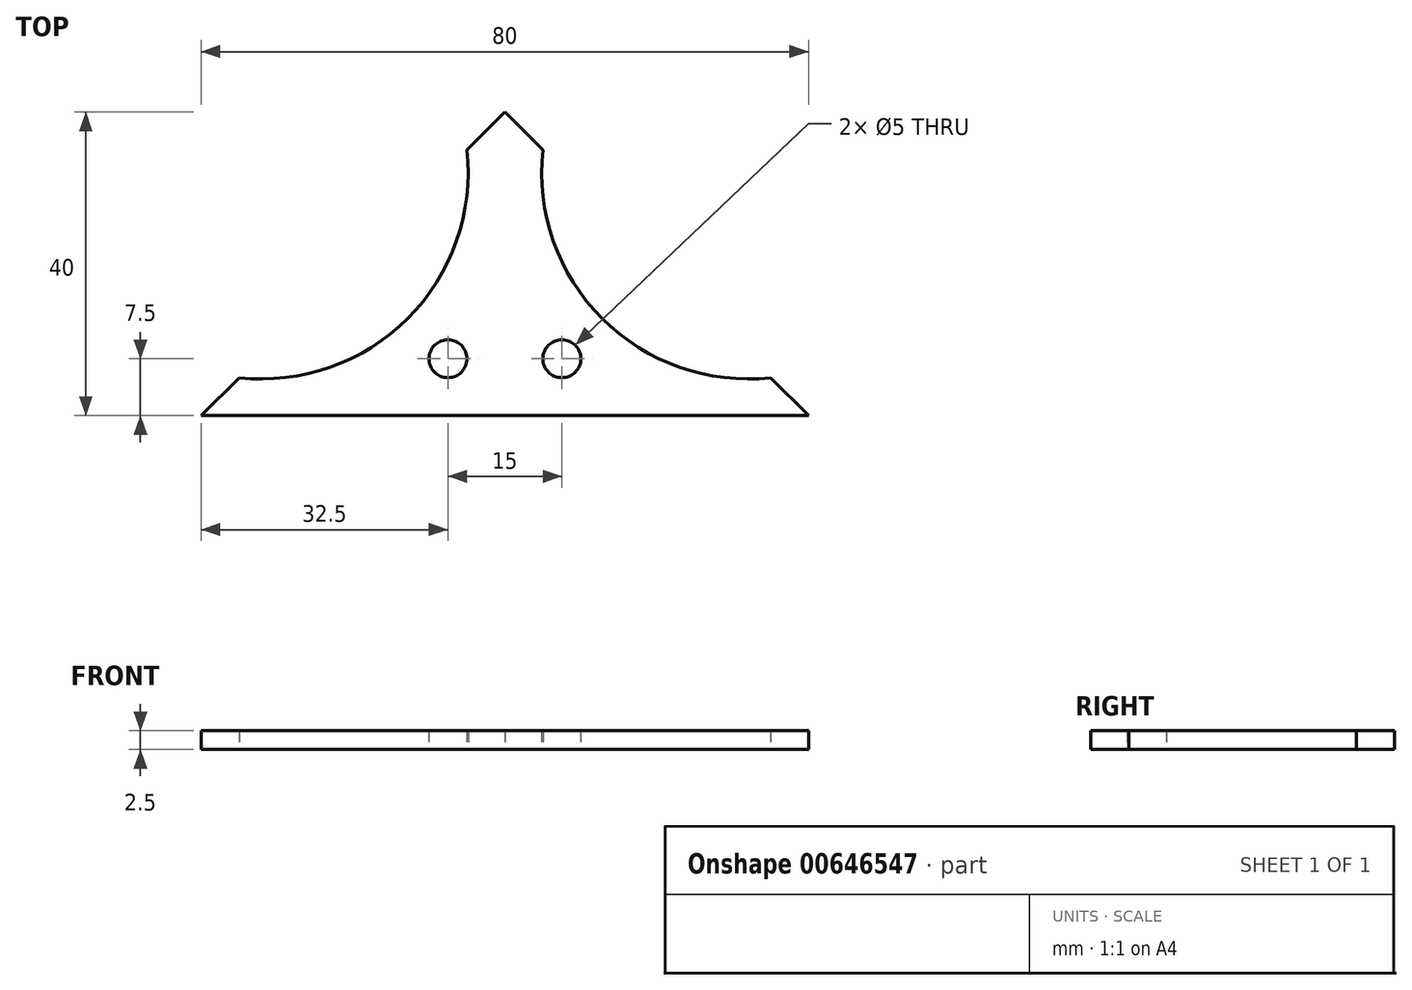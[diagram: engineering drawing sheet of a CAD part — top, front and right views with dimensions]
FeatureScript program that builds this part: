
annotation { "Feature Type Name" : "Feature", "Feature Type Description" : "" }
export const myFeature = defineFeature(function(context is Context, id is Id, definition is map)
    precondition{}
    {
        {
            var Q0;
            Q0=qCreatedBy(makeId("Top.planeOp"),FACE);
            var sketch = newSketch(context, id + "F0", { "sketchPlane" : qUnion([Q0])});
            skLineSegment(sketch, "E0", {"start": v(0, 20) * mm, "end": v(0, -20) * mm});
            skLineSegment(sketch, "E1", {"start": v(0, -20) * mm, "end": v(-40, -20) * mm});
            skLineSegment(sketch, "E2", {"start": v(-40, -20) * mm, "end": v(0, 20) * mm});
            skCircle(sketch, "E3", {"center": v(-7.5, -12.5) * mm, "radius": 2.5 * mm});
            skLineSegment(sketch, "E4", {"start": v(-25.6, -20) * mm, "end": v(0, 5.6) * mm, "construction": true});
            skPoint(sketch, "E5", {"position": v(-12.8, -7.2) * mm});
            skPoint(sketch, "E6", {"position": v(-35, -15) * mm});
            skPoint(sketch, "E7", {"position": v(-5, 15) * mm});
            skArc(sketch, "E8", {"start": v(-35, -15) * mm, "mid": v(-12.8, -7.2) * mm, "end": v(-5, 15) * mm});
            skSolve(sketch);
        }
        {
            var Q0;
            {var subQ1=sQuery(id+"F0.wireOp",EDGE,"E0");Q0=makeQuery(id+"F0.imprint","IMPRINT",FACE,{"disambiguationData":[TD([[makeQuery(id+"F0.imprint","IMPRINT",EDGE,{"derivedFrom":subQ1}),-1.0]])]});}
            extrude(context, id + "F1", {"entities" : qUnion([Q0]), "depth" : 2.5 * mm, "offsetDistance" : 25 * mm});
        }
        {
            var Q0;
            Q0=makeQuery(id+"F1.opExtrude","SWEPT_BODY",BODY,{"disambiguationData":[OSD([sQuery(id+"F0.wireOp",EDGE,"E0"),sQuery(id+"F0.wireOp",EDGE,"E1"),sQuery(id+"F0.wireOp",EDGE,"E2"),sQuery(id+"F0.wireOp",EDGE,"E3"),sQuery(id+"F0.wireOp",EDGE,"E8")])]});
            var Q1;
            Q1=makeQuery(id+"F1.opExtrude","SWEPT_FACE",FACE,{"disambiguationData":[OSD([sQuery(id+"F0.wireOp",EDGE,"E0")])]});
            mirror(context, id + "F2", {"operationType" : NewBodyOperationType.ADD, "entities" : qUnion([Q0]), "mirrorPlane" : qUnion([Q1])});
        }
    });
